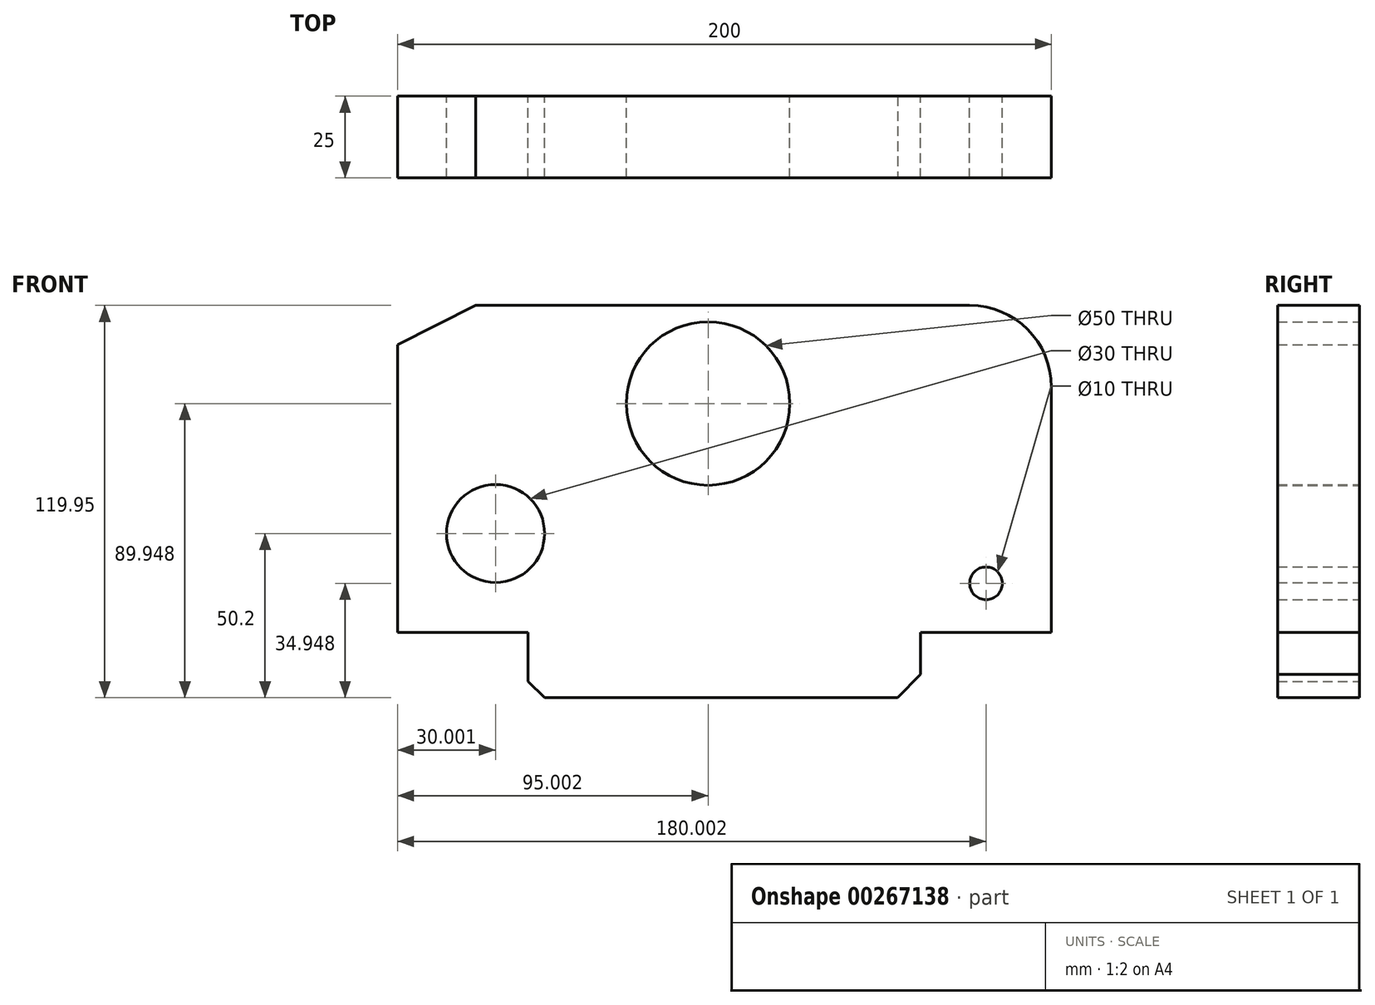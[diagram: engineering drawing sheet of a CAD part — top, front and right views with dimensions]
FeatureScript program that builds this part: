
annotation { "Feature Type Name" : "Feature", "Feature Type Description" : "" }
export const myFeature = defineFeature(function(context is Context, id is Id, definition is map)
    precondition{}
    {
        {
            var Q0;
            Q0=qCreatedBy(makeId("Front.planeOp"),FACE);
            var sketch = newSketch(context, id + "F0", { "sketchPlane" : qUnion([Q0])});
            skLineSegment(sketch, "E0", {"start": v(-53.33, 57.75) * mm, "end": v(-29.33, 69.75) * mm});
            skLineSegment(sketch, "E1", {"start": v(-53.33, 57.75) * mm, "end": v(-53.33, -0.25) * mm});
            skLineSegment(sketch, "E2", {"start": v(-53.33, -0.25) * mm, "end": v(-53.33, -30.25) * mm});
            skLineSegment(sketch, "E3", {"start": v(-53.33, -30.25) * mm, "end": v(-13.33, -30.25) * mm});
            skLineSegment(sketch, "E4", {"start": v(-13.33, -30.25) * mm, "end": v(-13.33, -45.2) * mm});
            skLineSegment(sketch, "E5", {"start": v(-13.33, -45.2) * mm, "end": v(-8.33, -50.2) * mm});
            skPoint(sketch, "E6.visualSharp", {"position": v(146.67, 69.75) * mm});
            skLineSegment(sketch, "E7", {"start": v(-8.33, -50.2) * mm, "end": v(106.67, -50.2) * mm});
            skLineSegment(sketch, "E8", {"start": v(-13.33, -30.25) * mm, "end": v(106.67, -30.25) * mm});
            skLineSegment(sketch, "E9", {"start": v(106.67, -50.2) * mm, "end": v(106.67, -30.25) * mm});
            skLineSegment(sketch, "E10", {"start": v(106.67, -30.25) * mm, "end": v(146.67, -30.25) * mm});
            skLineSegment(sketch, "E11", {"start": v(-29.33, 69.75) * mm, "end": v(121.67, 69.75) * mm});
            skLineSegment(sketch, "E12", {"start": v(146.67, 44.75) * mm, "end": v(146.67, -30.25) * mm});
            skArc(sketch, "E13.filletArc", {"start": v(146.67, 44.75) * mm, "mid": v(139.35, 62.43) * mm, "end": v(121.67, 69.75) * mm});
            skLineSegment(sketch, "E14", {"start": v(-29.33, 69.75) * mm, "end": v(41.67, 69.75) * mm});
            skLineSegment(sketch, "E15", {"start": v(41.67, 69.75) * mm, "end": v(41.67, 39.75) * mm});
            skCircle(sketch, "E16", {"center": v(41.67, 39.75) * mm, "radius": 25 * mm});
            skLineSegment(sketch, "E17", {"start": v(146.67, -30.25) * mm, "end": v(146.67, -15.25) * mm});
            skLineSegment(sketch, "E18", {"start": v(146.67, -15.25) * mm, "end": v(126.67, -15.25) * mm});
            skCircle(sketch, "E19", {"center": v(126.67, -15.25) * mm, "radius": 5 * mm});
            skLineSegment(sketch, "E20", {"start": v(-53.33, -30.25) * mm, "end": v(-33.33, -30.25) * mm});
            skLineSegment(sketch, "E21", {"start": v(-53.33, -30.25) * mm, "end": v(-53.33, -0.25) * mm});
            skLineSegment(sketch, "E22", {"start": v(-53.33, -0.25) * mm, "end": v(-23.33, 0) * mm});
            skCircle(sketch, "E23", {"center": v(-23.33, 0) * mm, "radius": 15 * mm});
            skSolve(sketch);
        }
        {
            var Q0;
            Q0=makeQuery(id+"F0.imprint","IMPRINT",FACE,{"disambiguationData":[TD([[makeQuery(id+"F0.imprint","IMPRINT",EDGE,{"derivedFrom":sQuery(id+"F0.wireOp",EDGE,"E0")}),-1.0]])]});
            var Q1;
            Q1=makeQuery(id+"F0.imprint","IMPRINT",FACE,{"disambiguationData":[TD([[makeQuery(id+"F0.imprint","IMPRINT",EDGE,{"derivedFrom":sQuery(id+"F0.wireOp",EDGE,"E4")}),1.0]])]});
            extrude(context, id + "F1", {"entities" : qUnion([Q0, Q1]), "depth" : 25 * mm});
        }
        {
            var Q0;
            Q0=makeQuery(id+"F1.opExtrude","SWEPT_EDGE",EDGE,{"disambiguationData":[OSD([sQuery(id+"F0.wireOp",EDGE,"E7"),sQuery(id+"F0.wireOp",EDGE,"E9")])]});
            chamfer(context, id + "F2", {"entities" : qUnion([Q0]), "width" : 7.07 * mm, "tangentPropagation" : true});
        }
    });
